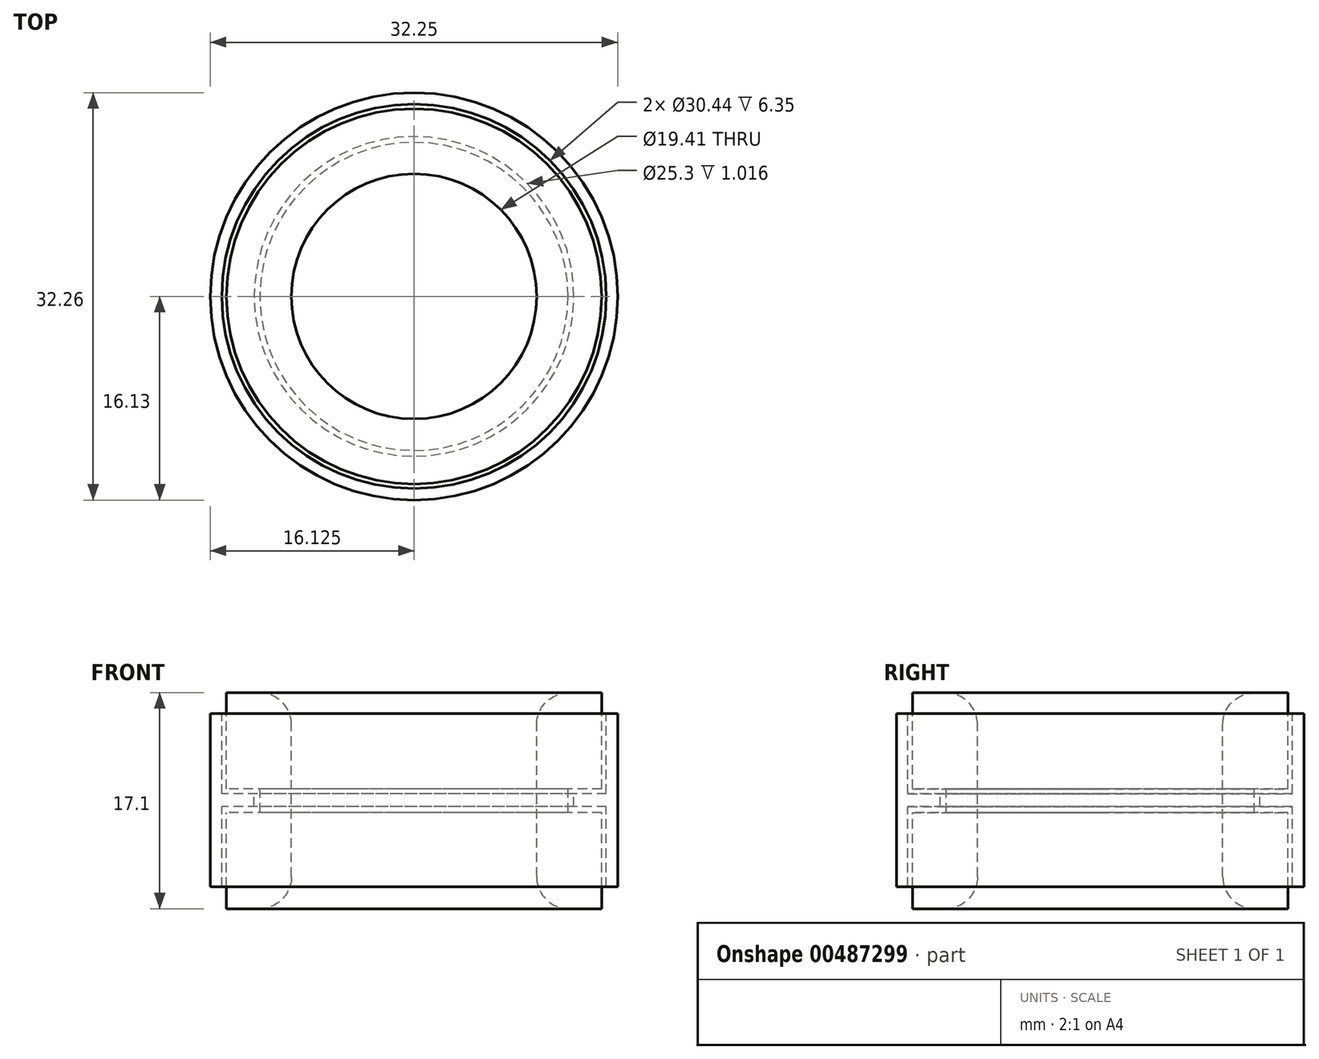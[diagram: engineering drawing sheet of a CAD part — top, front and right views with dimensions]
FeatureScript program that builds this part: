
annotation { "Feature Type Name" : "Feature", "Feature Type Description" : "" }
export const myFeature = defineFeature(function(context is Context, id is Id, definition is map)
    precondition{}
    {
        {
            var Q0;
            Q0=qCreatedBy(makeId("Front.planeOp"),FACE);
            var sketch = newSketch(context, id + "F0", { "sketchPlane" : qUnion([Q0])});
            skLineSegment(sketch, "E0", {"start": v(11.94, 11.88) * mm, "end": v(11.94, -7.74) * mm});
            skLineSegment(sketch, "E1", {"start": v(26.8, 11.16) * mm, "end": v(21.65, 11.16) * mm});
            skLineSegment(sketch, "E2", {"start": v(21.65, 11.16) * mm, "end": v(21.65, -5.94) * mm});
            skLineSegment(sketch, "E3", {"start": v(21.65, -5.94) * mm, "end": v(26.8, -5.94) * mm});
            skLineSegment(sketch, "E4", {"start": v(26.8, 11.16) * mm, "end": v(26.8, 3.54) * mm});
            skLineSegment(sketch, "E5", {"start": v(26.8, -5.94) * mm, "end": v(26.8, 1.68) * mm});
            skLineSegment(sketch, "E6", {"start": v(26.8, 3.54) * mm, "end": v(24.14, 3.54) * mm});
            skLineSegment(sketch, "E7", {"start": v(24.14, 3.54) * mm, "end": v(24.14, 1.68) * mm});
            skLineSegment(sketch, "E8", {"start": v(24.14, 1.68) * mm, "end": v(26.8, 1.68) * mm});
            skLineSegment(sketch, "E9", {"start": v(27.16, 9.51) * mm, "end": v(27.16, 3.16) * mm});
            skLineSegment(sketch, "E10", {"start": v(27.16, 3.16) * mm, "end": v(24.6, 3.16) * mm});
            skLineSegment(sketch, "E11", {"start": v(24.6, 3.16) * mm, "end": v(24.6, 2.14) * mm});
            skLineSegment(sketch, "E12", {"start": v(24.6, 2.14) * mm, "end": v(27.16, 2.14) * mm});
            skLineSegment(sketch, "E13", {"start": v(27.16, 2.14) * mm, "end": v(27.16, -4.2) * mm});
            skLineSegment(sketch, "E14", {"start": v(27.16, -4.2) * mm, "end": v(28.07, -4.2) * mm});
            skLineSegment(sketch, "E15", {"start": v(27.16, 9.51) * mm, "end": v(28.07, 9.51) * mm});
            skLineSegment(sketch, "E16", {"start": v(28.07, 9.51) * mm, "end": v(28.07, -4.2) * mm});
            skSolve(sketch);
        }
        {
            var Q0;
            Q0=makeQuery(id+"F0.imprint","IMPRINT",FACE,{"disambiguationData":[TD([[makeQuery(id+"F0.imprint","IMPRINT",EDGE,{"derivedFrom":sQuery(id+"F0.wireOp",EDGE,"E1")}),1.0]])]});
            var Q1;
            Q1=makeQuery(id+"F0.imprint","IMPRINT",FACE,{"disambiguationData":[TD([[makeQuery(id+"F0.imprint","IMPRINT",EDGE,{"derivedFrom":sQuery(id+"F0.wireOp",EDGE,"E9")}),1.0]])]});
            var Q2;
            Q2=sQuery(id+"F0.wireOp",EDGE,"E0");
            revolve(context, id + "F1", {"entities" : qUnion([Q0, Q1]), "axis" : qUnion([Q2]), "revolveType" : RevolveType.FULL});
        }
        {
            var Q0;
            Q0=makeQuery(id+"F1.opRevolve","SWEPT_EDGE",EDGE,{"disambiguationData":[OSD([sQuery(id+"F0.wireOp",EDGE,"E1"),sQuery(id+"F0.wireOp",EDGE,"E2")])]});
            var Q1;
            Q1=makeQuery(id+"F1.opRevolve","SWEPT_EDGE",EDGE,{"disambiguationData":[OSD([sQuery(id+"F0.wireOp",EDGE,"E2"),sQuery(id+"F0.wireOp",EDGE,"E3")])]});
            fillet(context, id + "F2", {"entities" : qUnion([Q0, Q1]), "radius" : 2.54 * mm, "tangentPropagation" : true, "allowEdgeOverflow" : false});
        }
    });
